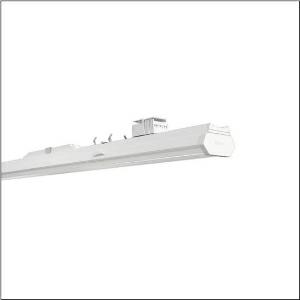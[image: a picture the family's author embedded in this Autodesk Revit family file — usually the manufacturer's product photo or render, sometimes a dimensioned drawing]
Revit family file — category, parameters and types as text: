
# Revit family: licross_r__11_protected_ho_51td11dn4f5s_b27d
name_source: partatom
category: Lighting Fixtures
units: mm (PartAtom-declared; Revit-internal decimal feet)

## family parameters
Cut with Voids When Loaded = No
Host = Face
Light Source = No
Part Type = Normal
Room Calculation Point = No
Round Connector Dimension = Use Diameter
Shared = No

## types (1)
- --- (1 x LED, 15510 lm, 87.3 W, 4000K)
    Apparent Load = 87 VA
    CIE Flux Codes = 84 94 98 99 100
    Color Rendering = 80
    Color Temperature = 4000K
    Default Elevation = 1800 mm
    Description = Licross® 11 Protected HO, luminaire insert, of sheet steel, galvanised, coil coated, white, length: 1.500mm, width: 90mm, height: 101mm, LED rated luminous flux: 15.510lm, light colour: 840, control gear: DALI 2, with plug, 5-pole, with phase selection, mains connection: 220..240V, AC, 50/60Hz, rated input power: 87W, halogen-free wiring, primary light control with lens, of plastic, primary optical cover: cover, of PMMA, light emission: direct distribution, primary light characteristic: symmetric, protection rating (complete): IP54, insulation class (complete): insulation class I (protective earthing), certification: CE, ENEC, VDE, UKCA, protection symbol: D if used in an environment with non-conductive dust loads with corresponding accessories, impact resistance: IK06, permissible ambient temperature for indoor applications: -25..+30°C, corresponds to IFS (International Featured Standards) requirements for safety and quality in the food industry, reducing of maximum allowable ambient temperature of 5°C with ceiling mounting, LABS conformity tested according to VDMA 24364:2018-05, packaging unit: 1 piece
    Height = 92 mm
    Lamp = 1 x LED
    Lamp Light Flux = 15510 lm
    Lamp Power = 87.3 W
    Lamp count = 1
    Length = 1500 mm
    Luminous efficacy = 178 lm/W
    Manufacturer = Siteco
    ModVariant = No
    Model = 51TD11DN4F5S
    Mounting Place = Ceiling
    Mounting Type = Pendant
    Number of Poles = 1
    OnlyDefault = Yes
    Power Factor = 1
    Product Name = Licross® 11 Protected HO
    Product group = luminaire insert
    ProductGroupID = 902
    Protection Class = Protection class I
    Protection Degree = IP 54
    RLX_Detail_Level = 1
    RLX_Emergency_Light_Flux = 0 lm
    RLX_Emergency_Type = 0
    RLX_Emergency_Type_DB = No
    RlxData = <blob elided: 24293 chars, md5=301fb807>
    Socket = socket
    Standby Power = 0 W
    System Light Flux = 15510 lm
    System Power = 87 W
    Type Comments = factory setting: luminous flux: 100 % | dim-lin: 254 | 589 mA
    Type Image = l_1256145.jpg
    URL = http://relux.com
    VarID = @adj_101098
    Voltage = 0 V
    Weight = 0.00 kg
    Width = 88 mm

## geometry (parser evidence)
native form markers: Blend x4, Sweep x9
no freeform markers — native parametric forms only
